# Revit family: KS Husky, Typ VI-32, M 8-M10, Ø 17,2- 48,3
name_source: partatom
category: HLS-Bauteile
revit_build: Autodesk Revit 2017 (Build: 20190507_1515(x64)
units: mm (PartAtom-declared; Revit-internal decimal feet)

## family parameters
Arbeitsebenenbasiert = Ja
Beim Laden mit Abzugskörper schneiden = Nein
Bemaßung runder Anschluss = Durchmesser verwenden
Gemeinsam genutzt = Ja
Immer vertikal = Nein
Raumberechnungspunkt = Nein
Teiletyp = Normal

## types (6) — shared parameters
Anschluss = M8/M10
Baustoffklasse = B2
DVS = 5 mm  [stored 0.0164042 ft]
Dichte Kern = 120 kg/m³
Dämmkörper = KA/PU
Fabrikat = MEFA
Firma = MEFA Befestigungs- und Montagesysteme GmbH
H1 = 2 mm  [stored 0.00656168 ft]
HGA = 16 mm  [stored 0.0524934 ft]
Kurztext1 = Kälteschelle Husky VI 32
L = 51 mm
MB = 25 mm  [stored 0.082021 ft]
Material = Stahl
Material Mantel = Kunststoff
Materialname = DD11
Mengeneinheit = St
Oberflaeche = galvanisch verzinkt
Rohrschellentyp = Trabant
Schalenlänge = 42 mm
Typ = VI 32
Vorgabe-Ansicht = 1219 mm
Wasserdampfdiffusionswiderstand = 7000 µ
Wärmeleitfähigkeit = 0.029 W/mK
max. Temperaturbeständigkeit = 105 °C
mittl. Nenndruckfestigkeit Kern = 1,35 N/mm²
stat. Belastung Kern = 0,27 N/mm²

## per-type parameters (varying)
- Kälteschelle Husky, Typ VI-32, M8/M10, Ø 17,2: A=48 mm  [stored 0.15748 ft]; Anschlußhöhe=49 mm; Artikelnummer=6850180; B=122 mm; Breite=121 mm; D=18 mm  [stored 0.0590551 ft]; D0=78 mm  [stored 0.255906 ft]; DF1=20 mm  [stored 0.0656168 ft]; DF2=21 mm  [stored 0.0688976 ft]; DS=30 mm  [stored 0.0984252 ft]; Dämmstärke=30 mm  [stored 0.0984252 ft]; EAN=4250928440976; Gewicht=0.15 kg; Gewicht pro Bauteil=0.15 kg; H=97 mm  [stored 0.318241 ft]; H2=3 mm  [stored 0.00984252 ft]; Kurztext2=17,2 mm Iso 30 x 42 mm M8/M10; MD=2 mm  [stored 0.00656168 ft]; R=39 mm  [stored 0.127953 ft]; RM=41 mm  [stored 0.134514 ft]; Rohraußendurchmesser Kunststoff=18 mm; Rohraußendurchmesser Kupfer=18 mm; Rohraußendurchmesser Stahl=17,2 mm; S=102 mm  [stored 0.334646 ft]; max. zul. Last=0.18 kN; vpe=12 St
- Kälteschelle Husky, Typ VI-32, M8/M10, Ø 21,3: A=48 mm  [stored 0.15748 ft]; Anschlußhöhe=49 mm; Artikelnummer=6850220; B=122 mm; Breite=121 mm; D=22 mm  [stored 0.0721785 ft]; D0=82 mm  [stored 0.269029 ft]; DF1=19 mm  [stored 0.062336 ft]; DF2=18 mm  [stored 0.0590551 ft]; DS=30 mm  [stored 0.0984252 ft]; Dämmstärke=30 mm  [stored 0.0984252 ft]; EAN=4250928440983; Gewicht=0.16 kg; Gewicht pro Bauteil=0.16 kg; H=101 mm  [stored 0.331365 ft]; H2=3 mm  [stored 0.00984252 ft]; Kurztext2=21,3 mm Iso 30 x 42 mm M8/M10; MD=2 mm  [stored 0.00656168 ft]; R=41 mm  [stored 0.134514 ft]; RM=43 mm; Rohraußendurchmesser Kupfer=22 mm; Rohraußendurchmesser Stahl=21,3 mm; S=103 mm  [stored 0.337927 ft]; max. zul. Last=0.22 kN; vpe=12 St
- Kälteschelle Husky, Typ VI-32, M8/M10, Ø 26,9: A=47 mm; Anschlußhöhe=48 mm; Artikelnummer=6850270; B=127 mm; Breite=124 mm; D=27 mm; D0=86 mm; DF1=19 mm  [stored 0.062336 ft]; DF2=19 mm  [stored 0.062336 ft]; DS=30 mm  [stored 0.0984252 ft]; Dämmstärke=30 mm  [stored 0.0984252 ft]; EAN=4250928440990; Gewicht=0.16 kg; Gewicht pro Bauteil=0.16 kg; H=105 mm; H2=3 mm  [stored 0.00984252 ft]; Kurztext2=26,9 mm Iso 30 x 42 mm M8/M10; MD=2 mm  [stored 0.00656168 ft]; R=43 mm; RM=45 mm; Rohraußendurchmesser Stahl=26,9 mm; S=108 mm; max. zul. Last=0.27 kN; vpe=12 St
- Kälteschelle Husky, Typ VI-32, M8/M10, Ø 33,7: A=50 mm  [stored 0.164042 ft]; Anschlußhöhe=50 mm; Artikelnummer=6850340; B=134 mm; Breite=134 mm; D=34 mm; D0=97 mm  [stored 0.318241 ft]; DF1=17 mm  [stored 0.0557743 ft]; DF2=16 mm  [stored 0.0524934 ft]; DS=32 mm  [stored 0.104987 ft]; Dämmstärke=32 mm  [stored 0.104987 ft]; EAN=4250928441003; Gewicht=0.22 kg; Gewicht pro Bauteil=0.22 kg; H=117 mm; H2=4 mm  [stored 0.0131234 ft]; Kurztext2=33,7 mm Iso 32 x 42 mm M8/M10; MD=2 mm  [stored 0.00656168 ft]; R=49 mm; RM=51 mm; Rohraußendurchmesser Stahl=33,7 mm; S=117 mm; max. zul. Last=0.33 kN; vpe=12 St
- Kälteschelle Husky, Typ VI-32, M8/M10, Ø 42,4: A=55 mm; Anschlußhöhe=56 mm; Artikelnummer=6850420; B=166 mm; Breite=165 mm; D=42 mm; D0=115 mm; DF1=23 mm  [stored 0.0754593 ft]; DF2=23 mm  [stored 0.0754593 ft]; DS=36 mm  [stored 0.11811 ft]; Dämmstärke=36 mm  [stored 0.11811 ft]; EAN=4250928441010; Gewicht=0.30 kg; Gewicht pro Bauteil=0.30 kg; H=136 mm; H2=4 mm  [stored 0.0131234 ft]; Kurztext2=42,4 mm Iso 36 x 42 mm M8/M10; MD=3 mm  [stored 0.00984252 ft]; R=58 mm  [stored 0.190289 ft]; RM=60 mm; Rohraußendurchmesser Stahl=42,4 mm; S=143 mm; max. zul. Last=0.42 kN; vpe=12 St
- Kälteschelle Husky, Typ VI-32, M8/M10, Ø 48,3: A=55 mm; Anschlußhöhe=56 mm; Artikelnummer=6850480; B=166 mm; Breite=165 mm; D=48 mm  [stored 0.15748 ft]; D0=121 mm; DF1=20 mm  [stored 0.0656168 ft]; DF2=20 mm  [stored 0.0656168 ft]; DS=36 mm  [stored 0.11811 ft]; Dämmstärke=36 mm  [stored 0.11811 ft]; EAN=4250928441027; Gewicht=0.31 kg; Gewicht pro Bauteil=0.31 kg; H=142 mm; H2=4 mm  [stored 0.0131234 ft]; Kurztext2=48,3 mm Iso 36 x 42 mm M8/M10; MD=3 mm  [stored 0.00984252 ft]; R=61 mm; RM=63 mm; Rohraußendurchmesser Stahl=48,3 mm; S=146 mm; max. zul. Last=0.48 kN; vpe=10 St

note: [stored X ft] marks values corroborated as IEEE doubles in the binary element streams (Revit-internal decimal feet)

## geometry (parser evidence)
native form markers: Sweep x1
no freeform markers — native parametric forms only
